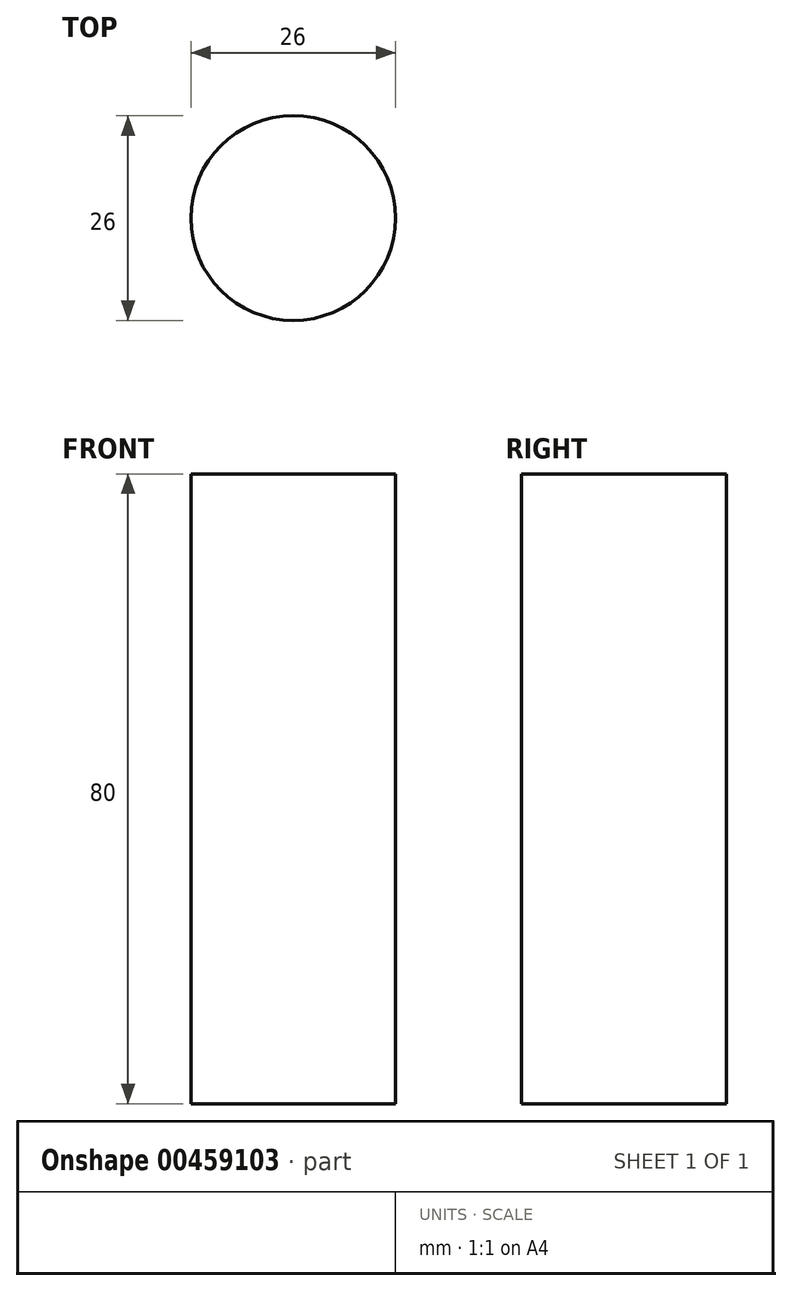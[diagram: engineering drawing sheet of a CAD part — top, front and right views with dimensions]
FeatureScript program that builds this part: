
annotation { "Feature Type Name" : "Feature", "Feature Type Description" : "" }
export const myFeature = defineFeature(function(context is Context, id is Id, definition is map)
    precondition{}
    {
        {
            var Q0;
            Q0=qCreatedBy(makeId("Top.planeOp"),FACE);
            var sketch = newSketch(context, id + "F0", { "sketchPlane" : qUnion([Q0])});
            skCircle(sketch, "E0", {"center": v(0, 0) * mm, "radius": 13 * mm});
            skSolve(sketch);
        }
        {
            var Q0;
            Q0=makeQuery(id+"F0.imprint","IMPRINT",FACE,{"disambiguationData":[TD([[makeQuery(id+"F0.imprint","IMPRINT",EDGE,{"derivedFrom":sQuery(id+"F0.wireOp",EDGE,"E0")}),1.0]])]});
            extrude(context, id + "F1", {"entities" : qUnion([Q0]), "depth" : 80 * mm});
        }
    });
